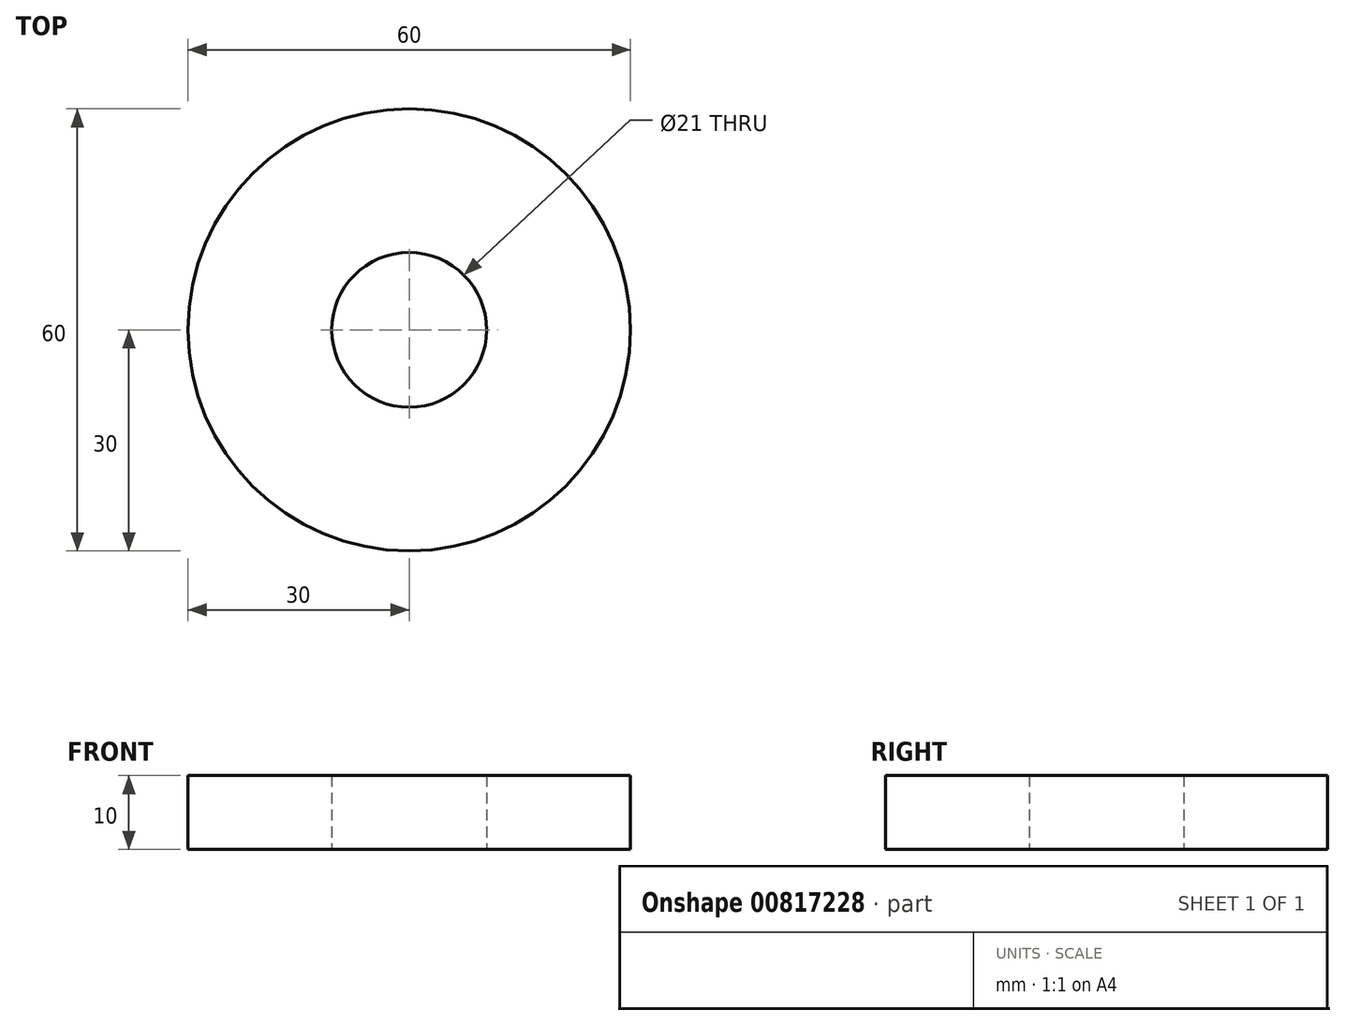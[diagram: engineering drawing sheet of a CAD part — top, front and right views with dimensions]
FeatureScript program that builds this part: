
annotation { "Feature Type Name" : "Feature", "Feature Type Description" : "" }
export const myFeature = defineFeature(function(context is Context, id is Id, definition is map)
    precondition{}
    {
        {
            var Q0;
            Q0=qCreatedBy(makeId("Top.planeOp"),FACE);
            var sketch = newSketch(context, id + "F0", { "sketchPlane" : qUnion([Q0])});
            skCircle(sketch, "E0", {"center": v(0, 0) * mm, "radius": 30 * mm});
            skCircle(sketch, "E1", {"center": v(0, 0) * mm, "radius": 10.5 * mm});
            skSolve(sketch);
        }
        {
            var Q0;
            Q0=makeQuery(id+"F0.imprint","IMPRINT",FACE,{"disambiguationData":[TD([[makeQuery(id+"F0.imprint","IMPRINT",EDGE,{"derivedFrom":sQuery(id+"F0.wireOp",EDGE,"E0")}),1.0]])]});
            extrude(context, id + "F1", {"entities" : qUnion([Q0]), "depth" : 10 * mm, "offsetDistance" : 25 * mm});
        }
    });
